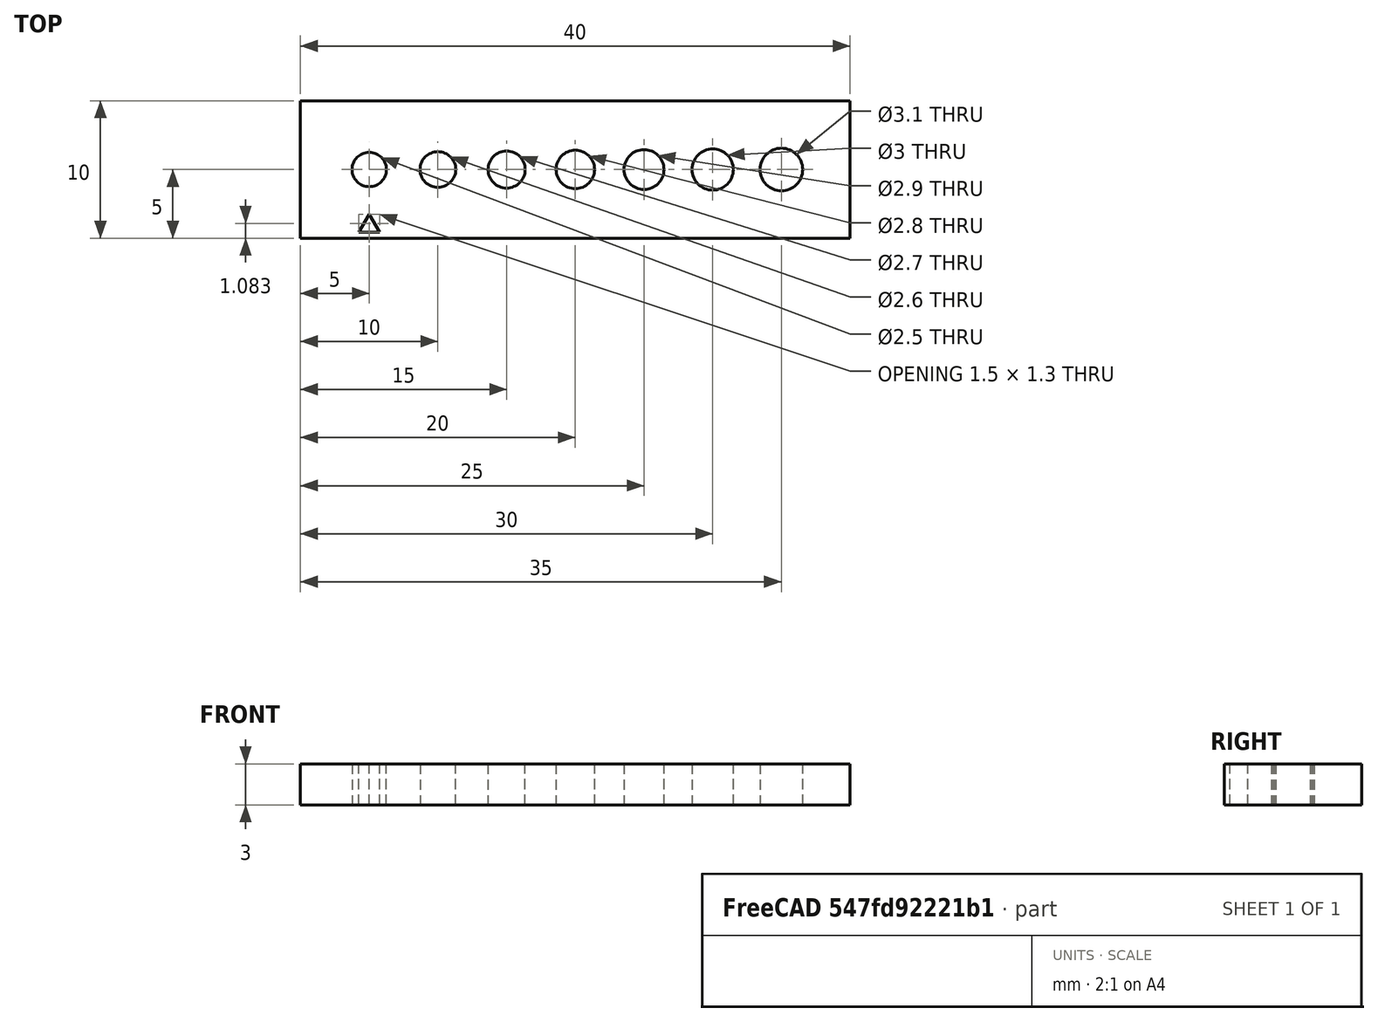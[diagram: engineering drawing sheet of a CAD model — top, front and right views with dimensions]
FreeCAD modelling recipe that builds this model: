
FCSTD DOCUMENT  (FreeCAD 0.18R16146 (Git))
Label: M3Trial
License: All rights reserved
LicenseURL: http://en.wikipedia.org/wiki/All_rights_reserved
objects: Sketcher::SketchObject×1, PartDesign::Pad×1, PartDesign::Body×1
note: 4 computed .brp shape members not serialized (recipe doc carries the construction recipe); baked Part::Feature solids carry a one-line shape summary decoded from their .brp

FEATURE [Sketcher::SketchObject] Sketch
  MapMode = 5
  Support = -> [XY_Plane]
  sketch-geometry (17):
    g0: LineSegment StartX=0 StartY=10 StartZ=0 EndX=40 EndY=10 EndZ=0
    g1: LineSegment StartX=40 StartY=10 StartZ=0 EndX=40 EndY=0 EndZ=0
    g2: LineSegment StartX=40 StartY=0 StartZ=0 EndX=0 EndY=0 EndZ=0
    g3: LineSegment StartX=0 StartY=0 StartZ=0 EndX=0 EndY=10 EndZ=0
    g4: Circle CenterX=5 CenterY=5 CenterZ=0 NormalX=0 NormalY=0 NormalZ=1 AngleXU=0 Radius=1.25
    g5: Circle CenterX=15 CenterY=5 CenterZ=0 NormalX=0 NormalY=0 NormalZ=1 AngleXU=0 Radius=1.35
    g6: Circle CenterX=10 CenterY=5 CenterZ=0 NormalX=0 NormalY=0 NormalZ=1 AngleXU=0 Radius=1.3
    g7: Circle CenterX=20 CenterY=5 CenterZ=0 NormalX=0 NormalY=0 NormalZ=1 AngleXU=0 Radius=1.4
    g8: Circle CenterX=25 CenterY=5 CenterZ=0 NormalX=0 NormalY=0 NormalZ=1 AngleXU=0 Radius=1.45
    g9: Circle CenterX=30 CenterY=5 CenterZ=0 NormalX=0 NormalY=0 NormalZ=1 AngleXU=0 Radius=1.5
    g10: Circle CenterX=35 CenterY=5 CenterZ=0 NormalX=0 NormalY=0 NormalZ=1 AngleXU=0 Radius=1.55
    g11: LineSegment [constr] StartX=0 StartY=5 StartZ=0 EndX=40 EndY=5 EndZ=0
    g12: LineSegment StartX=4.25 StartY=0.433013 StartZ=0 EndX=5.75 EndY=0.433013 EndZ=0
    g13: LineSegment StartX=5.75 StartY=0.433013 StartZ=0 EndX=5 EndY=1.73205 EndZ=0
    g14: LineSegment StartX=5 StartY=1.73205 StartZ=0 EndX=4.25 EndY=0.433013 EndZ=0
    g15: Circle [constr] CenterX=5 CenterY=0.866025 CenterZ=0 NormalX=0 NormalY=0 NormalZ=1 AngleXU=0 Radius=0.866025
    g16: LineSegment [constr] StartX=5 StartY=5 StartZ=0 EndX=5 EndY=0 EndZ=0
  constraints (51):
    c: Coincident(g0,g1)
    c: Coincident(g1,g2)
    c: Coincident(g2,g3)
    c: Coincident(g3,g0)
    c: Horizontal(g0)
    c: Horizontal(g2)
    c: Vertical(g1)
    c: Vertical(g3)
    c: Coincident(g2,g-1)
    c: Distance(g0,g0) = 40
    c: Distance(g0,g1) = 10
    c: Radius(g4) = 1.25
    c: Radius(g5) = 1.35
    c: Radius(g6) = 1.3
    c: Radius(g7) = 1.4
    c: Radius(g8) = 1.45
    c: Radius(g9) = 1.5
    c: Radius(g10) = 1.55
    c: PointOnObject(g11,g3)
    c: PointOnObject(g11,g1)
    c: Horizontal(g11)
    c: DistanceY(g2,g11) = 5
    c: PointOnObject(g4,g11)
    c: PointOnObject(g6,g11)
    c: PointOnObject(g5,g11)
    c: PointOnObject(g7,g11)
    c: PointOnObject(g8,g11)
    c: PointOnObject(g9,g11)
    c: PointOnObject(g10,g11)
    c: Distance(g4,g11) = 5
    c: Distance(g6,g4) = 5
    c: Distance(g6,g5) = 5
    c: Distance(g7,g5) = 5
    c: Distance(g8,g7) = 5
    c: Distance(g9,g8) = 5
    c: Distance(g10,g9) = 5
    c: Coincident(g12,g13)
    c: Coincident(g13,g14)
    c: Coincident(g14,g12)
    c: Equal(g12,g13)
    c: Equal(g12,g14)
    c: PointOnObject(g12,g15)
    c: PointOnObject(g13,g15)
    c: PointOnObject(g14,g15)
    c: Distance(g13) = 1.5
    c: Coincident(g16,g4)
    c: PointOnObject(g16,g2)
    c: Vertical(g16)
    c: PointOnObject(g13,g16)
    c: PointOnObject(g15,g16)
    c: Tangent(g15,g2)
FEATURE [PartDesign::Pad] Pad
  Length = 3
  Length2 = 100
  Profile = -> Sketch
  Type = 0
FEATURE [PartDesign::Body] Body
  Group = -> [Sketch,Pad]
  Origin = -> Origin
  Tip = -> Pad
